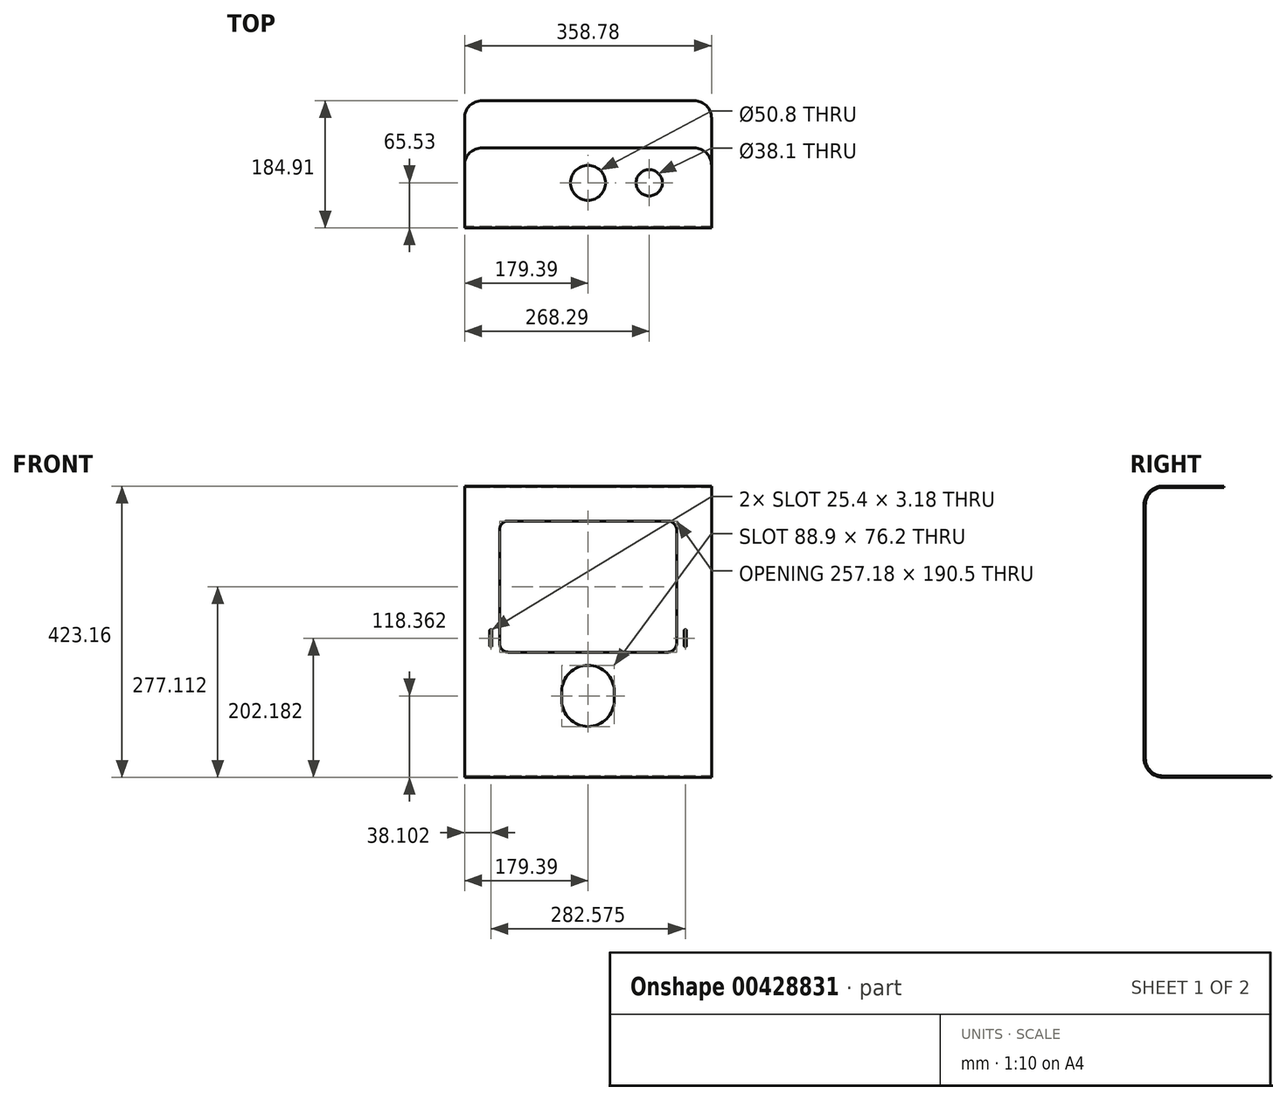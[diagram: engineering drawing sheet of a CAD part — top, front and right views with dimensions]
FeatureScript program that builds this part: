
annotation { "Feature Type Name" : "Feature", "Feature Type Description" : "" }
export const myFeature = defineFeature(function(context is Context, id is Id, definition is map)
    precondition{}
    {
        {
            var Q0;
            Q0=qCreatedBy(makeId("Right.planeOp"),FACE);
            var sketch = newSketch(context, id + "F0", { "sketchPlane" : qUnion([Q0])});
            skLineSegment(sketch, "E0", {"start": v(0, 184.15) * mm, "end": v(0, -184.15) * mm});
            skLineSegment(sketch, "E1", {"start": v(25.4, -209.55) * mm, "end": v(182.88, -209.55) * mm});
            skLineSegment(sketch, "E2", {"start": v(25.4, 209.55) * mm, "end": v(114.3, 209.55) * mm});
            skPoint(sketch, "E3.visualSharp", {"position": v(0, 209.55) * mm});
            skArc(sketch, "E3.filletArc", {"start": v(25.4, 209.55) * mm, "mid": v(7.44, 202.11) * mm, "end": v(0, 184.15) * mm});
            skPoint(sketch, "E4.visualSharp", {"position": v(0, -209.55) * mm});
            skArc(sketch, "E4.filletArc", {"start": v(0, -184.15) * mm, "mid": v(7.44, -202.11) * mm, "end": v(25.4, -209.55) * mm});
            skLineSegment(sketch, "E5.0", {"start": v(25.4, 211.58) * mm, "end": v(114.3, 211.58) * mm});
            skLineSegment(sketch, "E5.1", {"start": v(25.4, -211.58) * mm, "end": v(182.88, -211.58) * mm});
            skArc(sketch, "E5.2", {"start": v(-2.03, -184.15) * mm, "mid": v(6, -203.55) * mm, "end": v(25.4, -211.58) * mm});
            skLineSegment(sketch, "E5.3", {"start": v(-2.03, 184.15) * mm, "end": v(-2.03, -184.15) * mm});
            skArc(sketch, "E5.4", {"start": v(25.4, 211.58) * mm, "mid": v(6, 203.55) * mm, "end": v(-2.03, 184.15) * mm});
            skLineSegment(sketch, "E6", {"start": v(114.3, 211.58) * mm, "end": v(114.3, 209.55) * mm});
            skLineSegment(sketch, "E7", {"start": v(182.88, -209.55) * mm, "end": v(182.88, -211.58) * mm});
            skSolve(sketch);
        }
        {
            var Q0;
            Q0 = qSketchRegion(id + "F0", true);
            extrude(context, id + "F1", {"entities" : qUnion([Q0]), "endBound" : BoundingType.SYMMETRIC, "depth" : 358.77 * mm});
        }
        {
            var Q0;
            Q0=makeQuery(id+"F1.opExtrude","CAP_EDGE",EDGE,{"disambiguationData":[OSD([sQuery(id+"F0.wireOp",EDGE,"E6")])],"isStart":false});
            var Q1;
            Q1=makeQuery(id+"F1.opExtrude","CAP_EDGE",EDGE,{"disambiguationData":[OSD([sQuery(id+"F0.wireOp",EDGE,"E6")])],"isStart":true});
            var Q2;
            Q2=makeQuery(id+"F1.opExtrude","CAP_EDGE",EDGE,{"disambiguationData":[OSD([sQuery(id+"F0.wireOp",EDGE,"E7")])],"isStart":true});
            var Q3;
            Q3=makeQuery(id+"F1.opExtrude","CAP_EDGE",EDGE,{"disambiguationData":[OSD([sQuery(id+"F0.wireOp",EDGE,"E7")])],"isStart":false});
            fillet(context, id + "F2", {"entities" : qUnion([Q0, Q1, Q2, Q3]), "radius" : 25.4 * mm, "tangentPropagation" : true, "allowEdgeOverflow" : false});
        }
        {
            var Q0;
            Q0=makeQuery(id+"F1.opExtrude","SWEPT_FACE",FACE,{"disambiguationData":[OSD([sQuery(id+"F0.wireOp",EDGE,"E5.3")])]});
            var sketch = newSketch(context, id + "F3", { "sketchPlane" : qUnion([Q0])});
            skLineSegment(sketch, "E8.bottom", {"start": v(-115.89, 160.78) * mm, "end": v(115.89, 160.78) * mm});
            skLineSegment(sketch, "E8.top", {"start": v(-115.89, -29.72) * mm, "end": v(115.89, -29.72) * mm});
            skLineSegment(sketch, "E8.left", {"start": v(-128.59, 148.08) * mm, "end": v(-128.59, -17.02) * mm});
            skLineSegment(sketch, "E8.right", {"start": v(128.59, 148.08) * mm, "end": v(128.59, -17.02) * mm});
            skPoint(sketch, "E9.visualSharp", {"position": v(-128.59, 160.78) * mm});
            skArc(sketch, "E9.filletArc", {"start": v(-115.89, 160.78) * mm, "mid": v(-124.87, 157.06) * mm, "end": v(-128.59, 148.08) * mm});
            skPoint(sketch, "E10.visualSharp", {"position": v(128.59, 160.78) * mm});
            skArc(sketch, "E10.filletArc", {"start": v(128.59, 148.08) * mm, "mid": v(124.87, 157.06) * mm, "end": v(115.89, 160.78) * mm});
            skPoint(sketch, "E11.visualSharp", {"position": v(128.59, -29.72) * mm});
            skArc(sketch, "E11.filletArc", {"start": v(115.89, -29.72) * mm, "mid": v(124.87, -26) * mm, "end": v(128.59, -17.02) * mm});
            skPoint(sketch, "E12.visualSharp", {"position": v(-128.59, -29.72) * mm});
            skArc(sketch, "E12.filletArc", {"start": v(-128.59, -17.02) * mm, "mid": v(-124.87, -26) * mm, "end": v(-115.89, -29.72) * mm});
            skSolve(sketch);
        }
        {
            var Q0;
            Q0 = qSketchRegion(id + "F3", true);
            extrude(context, id + "F4", {"entities" : qUnion([Q0]), "operationType" : NewBodyOperationType.REMOVE, "oppositeDirection" : true, "depth" : 2.03 * mm});
        }
        {
            var Q0;
            Q0=makeQuery(id+"F1.opExtrude","SWEPT_FACE",FACE,{"disambiguationData":[OSD([sQuery(id+"F0.wireOp",EDGE,"E5.3")])]});
            var sketch = newSketch(context, id + "F5", { "sketchPlane" : qUnion([Q0])});
            skArc(sketch, "E13", {"start": v(38.1, -86.87) * mm, "mid": v(0, -48.77) * mm, "end": v(-38.1, -86.87) * mm});
            skArc(sketch, "E14", {"start": v(-38.1, -99.57) * mm, "mid": v(0, -137.67) * mm, "end": v(38.1, -99.57) * mm});
            skLineSegment(sketch, "E15", {"start": v(-38.1, -86.87) * mm, "end": v(-38.1, -99.57) * mm});
            skLineSegment(sketch, "E16", {"start": v(38.1, -86.87) * mm, "end": v(38.1, -99.57) * mm});
            skSolve(sketch);
        }
        {
            var Q0;
            Q0 = qSketchRegion(id + "F5", true);
            extrude(context, id + "F6", {"entities" : qUnion([Q0]), "operationType" : NewBodyOperationType.REMOVE, "oppositeDirection" : true, "depth" : 2.03 * mm});
        }
        {
            var Q0;
            Q0=makeQuery(id+"F1.opExtrude","SWEPT_FACE",FACE,{"disambiguationData":[OSD([sQuery(id+"F0.wireOp",EDGE,"E5.3")])]});
            var sketch = newSketch(context, id + "F7", { "sketchPlane" : qUnion([Q0])});
            skLineSegment(sketch, "E17.left", {"start": v(139.7, 1.71) * mm, "end": v(139.7, -20.51) * mm});
            skLineSegment(sketch, "E17.right", {"start": v(142.87, 1.71) * mm, "end": v(142.87, -20.51) * mm});
            skArc(sketch, "E18", {"start": v(142.87, 1.71) * mm, "mid": v(141.29, 3.3) * mm, "end": v(139.7, 1.71) * mm});
            skArc(sketch, "E19", {"start": v(139.7, -20.51) * mm, "mid": v(141.29, -22.1) * mm, "end": v(142.87, -20.51) * mm});
            skLineSegment(sketch, "E20.left", {"start": v(-142.88, 1.71) * mm, "end": v(-142.88, -20.51) * mm});
            skLineSegment(sketch, "E20.right", {"start": v(-139.7, 1.71) * mm, "end": v(-139.7, -20.51) * mm});
            skArc(sketch, "E21", {"start": v(-139.7, 1.71) * mm, "mid": v(-141.29, 3.3) * mm, "end": v(-142.87, 1.71) * mm});
            skArc(sketch, "E22", {"start": v(-142.87, -20.51) * mm, "mid": v(-141.29, -22.1) * mm, "end": v(-139.7, -20.51) * mm});
            skSolve(sketch);
        }
        {
            var Q0;
            Q0=makeQuery(id+"F7.imprint","IMPRINT",FACE,{"disambiguationData":[TD([[makeQuery(id+"F7.imprint","IMPRINT",EDGE,{"derivedFrom":sQuery(id+"F7.wireOp",EDGE,"E17.left")}),1.0]])]});
            var Q1;
            Q1=makeQuery(id+"F7.imprint","IMPRINT",FACE,{"disambiguationData":[TD([[makeQuery(id+"F7.imprint","IMPRINT",EDGE,{"derivedFrom":sQuery(id+"F7.wireOp",EDGE,"E20.left")}),1.0]])]});
            extrude(context, id + "F8", {"entities" : qUnion([Q0, Q1]), "operationType" : NewBodyOperationType.REMOVE, "oppositeDirection" : true, "depth" : 2.54 * mm});
        }
        {
            var Q0;
            Q0=makeQuery(id+"F1.opExtrude","SWEPT_FACE",FACE,{"disambiguationData":[OSD([sQuery(id+"F0.wireOp",EDGE,"E5.0")])]});
            var sketch = newSketch(context, id + "F9", { "sketchPlane" : qUnion([Q0])});
            skCircle(sketch, "E23", {"center": v(0, 63.5) * mm, "radius": 25.4 * mm});
            skSolve(sketch);
        }
        {
            var Q0;
            Q0 = qSketchRegion(id + "F9", true);
            extrude(context, id + "F10", {"entities" : qUnion([Q0]), "operationType" : NewBodyOperationType.REMOVE, "oppositeDirection" : true, "depth" : 25.4 * mm});
        }
        {
            var Q0;
            Q0=makeQuery(id+"F1.opExtrude","SWEPT_FACE",FACE,{"disambiguationData":[OSD([sQuery(id+"F0.wireOp",EDGE,"E5.0")])]});
            var sketch = newSketch(context, id + "F11", { "sketchPlane" : qUnion([Q0])});
            skCircle(sketch, "E24", {"center": v(88.9, 63.5) * mm, "radius": 19.05 * mm});
            skSolve(sketch);
        }
        {
            var Q0;
            Q0 = qSketchRegion(id + "F11", true);
            extrude(context, id + "F12", {"entities" : qUnion([Q0]), "operationType" : NewBodyOperationType.REMOVE, "oppositeDirection" : true, "depth" : 25.4 * mm});
        }
    });
